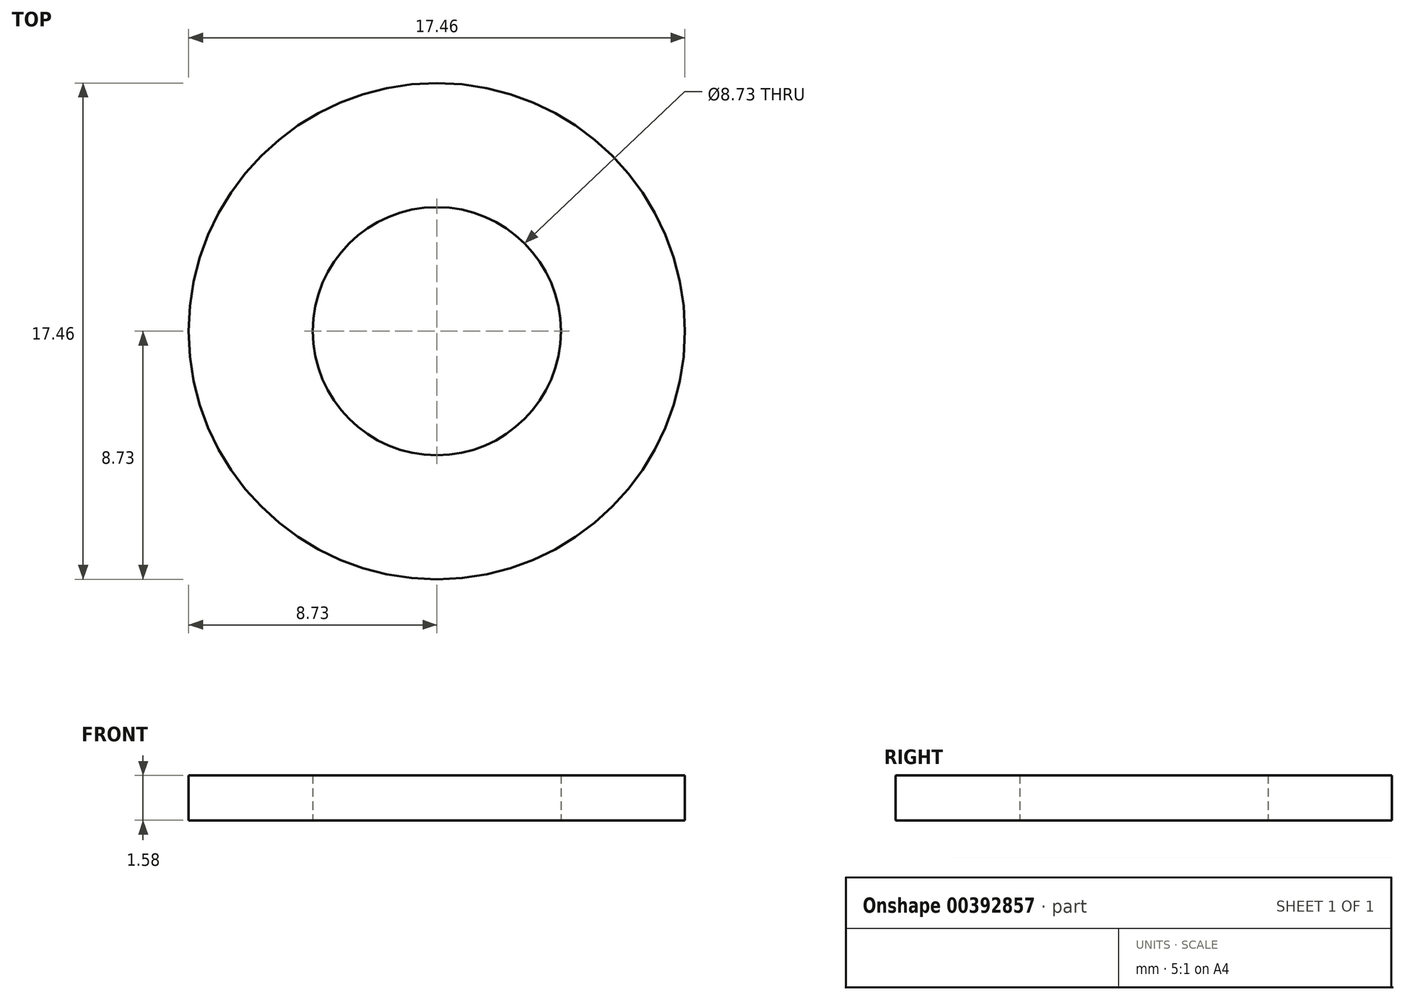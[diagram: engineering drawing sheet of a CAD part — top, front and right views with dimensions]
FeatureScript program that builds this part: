
annotation { "Feature Type Name" : "Feature", "Feature Type Description" : "" }
export const myFeature = defineFeature(function(context is Context, id is Id, definition is map)
    precondition{}
    {
        {
            var Q0;
            Q0=qCreatedBy(makeId("Front.planeOp"),FACE);
            var sketch = newSketch(context, id + "F0", { "sketchPlane" : qUnion([Q0])});
            skLineSegment(sketch, "E0.bottom", {"start": v(-4.37, -0.8) * mm, "end": v(-8.73, -0.8) * mm});
            skLineSegment(sketch, "E0.top", {"start": v(-4.37, 0.8) * mm, "end": v(-8.73, 0.8) * mm});
            skLineSegment(sketch, "E0.left", {"start": v(-4.37, -0.8) * mm, "end": v(-4.37, 0.8) * mm});
            skLineSegment(sketch, "E0.right", {"start": v(-8.73, -0.8) * mm, "end": v(-8.73, 0.8) * mm});
            skPoint(sketch, "E0.middle", {"position": v(-6.55, 0) * mm});
            skLineSegment(sketch, "E1", {"start": v(0, -5.61) * mm, "end": v(0, 21.29) * mm, "construction": true});
            skSolve(sketch);
        }
        {
            var Q0;
            Q0 = qSketchRegion(id + "F0", true);
            var Q1;
            Q1=sQuery(id+"F0.wireOp",EDGE,"E1");
            revolve(context, id + "F1", {"surfaceOperationType" : NewSurfaceOperationType.NEW, "entities" : qUnion([Q0]), "axis" : qUnion([Q1]), "revolveType" : RevolveType.FULL});
        }
    });
